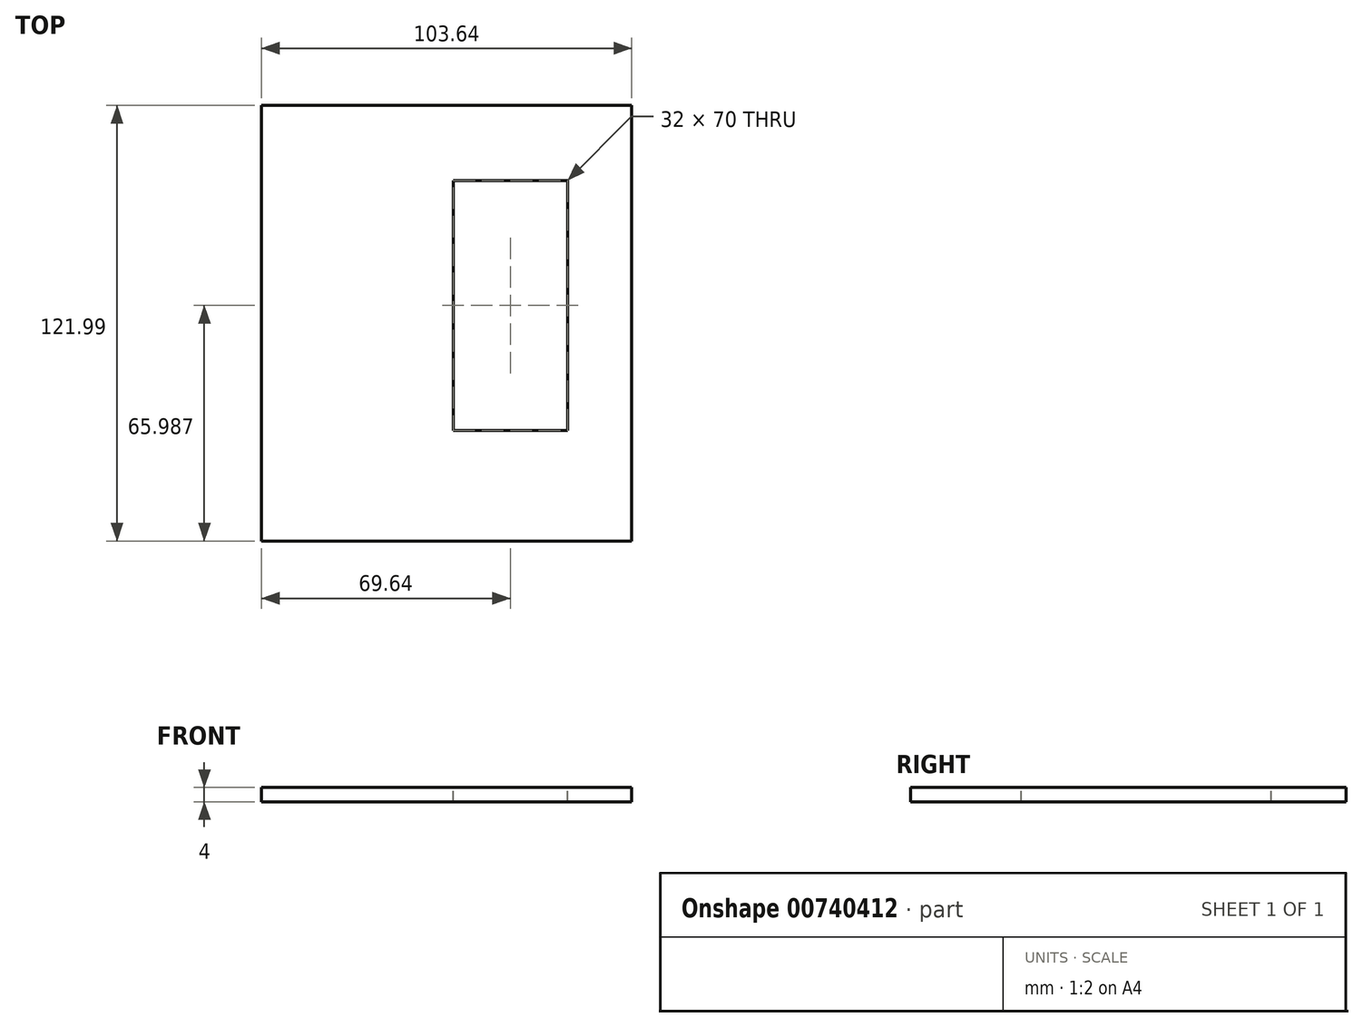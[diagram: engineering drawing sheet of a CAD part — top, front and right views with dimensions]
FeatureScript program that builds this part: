
annotation { "Feature Type Name" : "Feature", "Feature Type Description" : "" }
export const myFeature = defineFeature(function(context is Context, id is Id, definition is map)
    precondition{}
    {
        {
            var Q0;
            Q0=qCreatedBy(makeId("Top.planeOp"),FACE);
            var sketch = newSketch(context, id + "F0", { "sketchPlane" : qUnion([Q0])});
            skLineSegment(sketch, "E0.bottom", {"start": v(0, 0) * mm, "end": v(103.64, 0) * mm});
            skLineSegment(sketch, "E0.top", {"start": v(0, 121.99) * mm, "end": v(103.64, 121.99) * mm});
            skLineSegment(sketch, "E0.left", {"start": v(0, 0) * mm, "end": v(0, 121.99) * mm});
            skLineSegment(sketch, "E0.right", {"start": v(103.64, 0) * mm, "end": v(103.64, 121.99) * mm});
            skSolve(sketch);
        }
        {
            var Q0;
            Q0=qSketchRegion(id+"F0",true);
            extrude(context, id + "F1", {"entities" : qUnion([Q0]), "depth" : 4 * mm, "offsetDistance" : 25 * mm});
        }
        {
            var Q0;
            Q0=makeQuery(id+"F1.opExtrude","CAP_FACE",FACE,{"disambiguationData":[OSD([sQuery(id+"F0.wireOp",EDGE,"E0.bottom"),sQuery(id+"F0.wireOp",EDGE,"E0.top"),sQuery(id+"F0.wireOp",EDGE,"E0.left"),sQuery(id+"F0.wireOp",EDGE,"E0.right")])],"isStart":false});
            var sketch = newSketch(context, id + "F2", { "sketchPlane" : qUnion([Q0])});
            skLineSegment(sketch, "E1.bottom", {"start": v(53.64, 100.99) * mm, "end": v(85.64, 100.99) * mm});
            skLineSegment(sketch, "E1.top", {"start": v(53.64, 30.99) * mm, "end": v(85.64, 30.99) * mm});
            skLineSegment(sketch, "E1.left", {"start": v(53.64, 100.99) * mm, "end": v(53.64, 30.99) * mm});
            skLineSegment(sketch, "E1.right", {"start": v(85.64, 100.99) * mm, "end": v(85.64, 30.99) * mm});
            skLineSegment(sketch, "E2", {"start": v(69.64, 121.99) * mm, "end": v(69.64, 100.99) * mm, "construction": true});
            skSolve(sketch);
        }
        {
            var Q0;
            Q0=makeQuery(id+"F2.imprint","IMPRINT",FACE,{"disambiguationData":[TD([[makeQuery(id+"F2.imprint","IMPRINT",EDGE,{"derivedFrom":sQuery(id+"F2.wireOp",EDGE,"E1.bottom")}),-1.0]])]});
            extrude(context, id + "F3", {"entities" : qUnion([Q0]), "operationType" : NewBodyOperationType.REMOVE, "oppositeDirection" : true, "depth" : 25 * mm, "offsetDistance" : 25 * mm});
        }
    });
